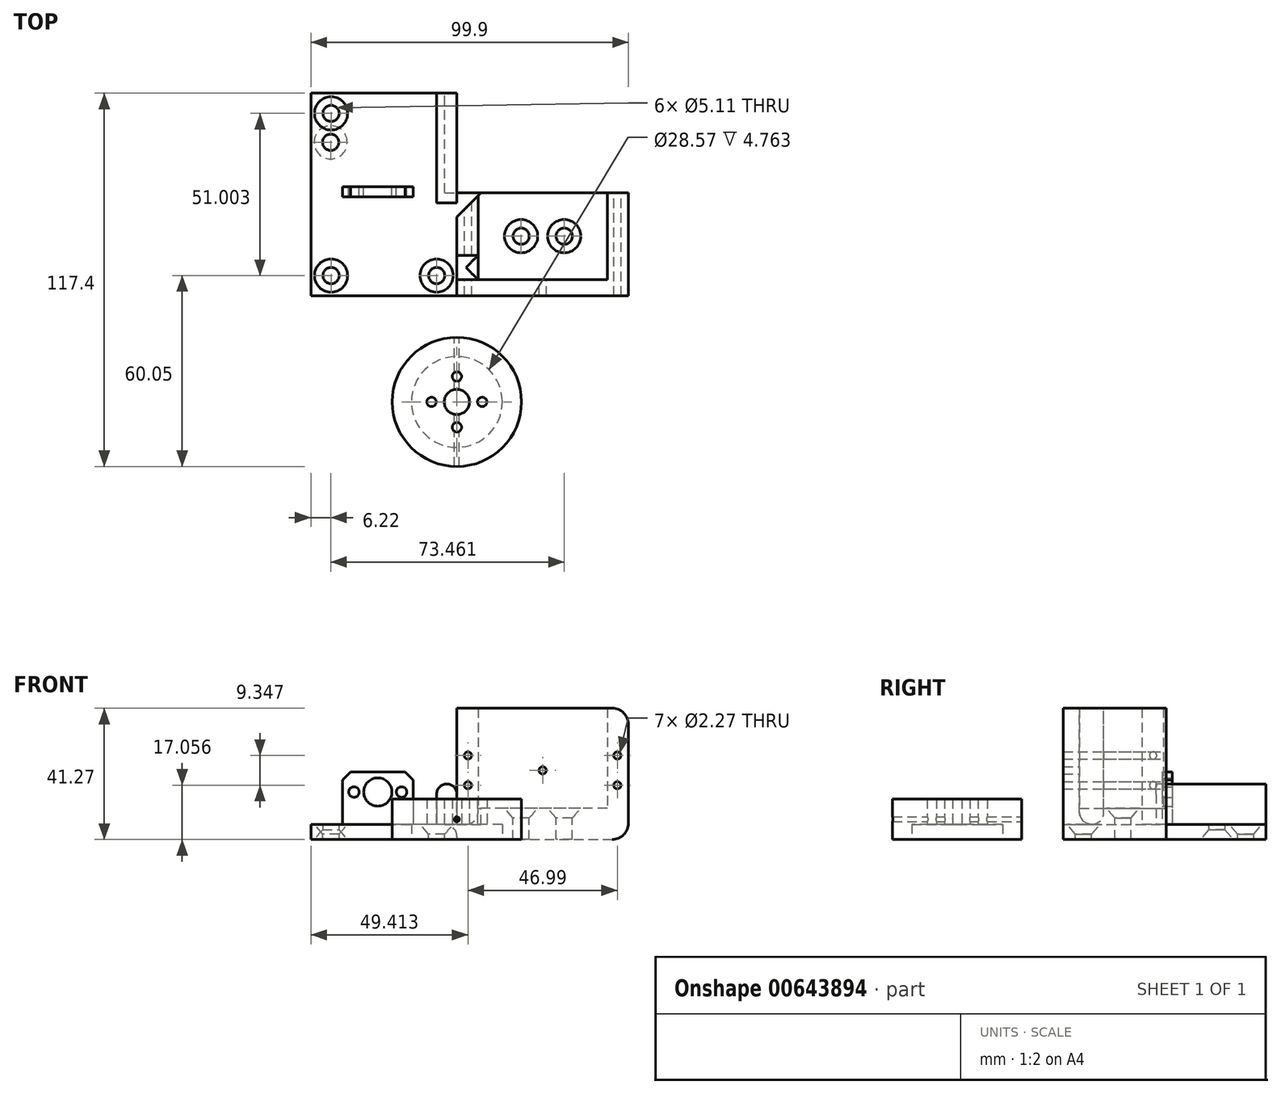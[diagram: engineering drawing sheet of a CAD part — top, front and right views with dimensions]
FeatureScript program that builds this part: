
annotation { "Feature Type Name" : "Feature", "Feature Type Description" : "" }
export const myFeature = defineFeature(function(context is Context, id is Id, definition is map)
    precondition{}
    {
        {
            var Q0;
            Q0=qCreatedBy(makeId("Top.planeOp"),FACE);
            var sketch = newSketch(context, id + "F0", { "sketchPlane" : qUnion([Q0])});
            skLineSegment(sketch, "E0.bottom", {"start": v(0, 0) * mm, "end": v(-45.92, 0) * mm});
            skLineSegment(sketch, "E0.top", {"start": v(0, 63.7) * mm, "end": v(-45.92, 63.7) * mm});
            skLineSegment(sketch, "E0.left", {"start": v(0, 0) * mm, "end": v(0, 63.7) * mm});
            skLineSegment(sketch, "E0.right", {"start": v(-45.92, 0) * mm, "end": v(-45.92, 63.7) * mm});
            skLineSegment(sketch, "E1.bottom", {"start": v(0, 32.38) * mm, "end": v(53.98, 32.38) * mm});
            skLineSegment(sketch, "E1.top", {"start": v(0, 0) * mm, "end": v(53.97, 0) * mm});
            skLineSegment(sketch, "E1.left", {"start": v(0, 32.38) * mm, "end": v(0, 0) * mm});
            skLineSegment(sketch, "E1.right", {"start": v(53.97, 32.38) * mm, "end": v(53.97, 0) * mm});
            skSolve(sketch);
        }
        {
            var Q0;
            Q0=makeQuery(id+"F0.imprint","IMPRINT",FACE,{"disambiguationData":[TD([[makeQuery(id+"F0.imprint","IMPRINT",EDGE,{"derivedFrom":sQuery(id+"F0.wireOp",EDGE,"E1.bottom")}),-1.0]])]});
            extrude(context, id + "F1", {"entities" : qUnion([Q0]), "depth" : 41.27 * mm, "offsetDistance" : 25.4 * mm});
        }
        {
            var Q0;
            Q0=makeQuery(id+"F0.imprint","IMPRINT",FACE,{"disambiguationData":[TD([[makeQuery(id+"F0.imprint","IMPRINT",EDGE,{"derivedFrom":sQuery(id+"F0.wireOp",EDGE,"E0.bottom")}),-1.0]])]});
            extrude(context, id + "F2", {"entities" : qUnion([Q0]), "operationType" : NewBodyOperationType.ADD, "depth" : 4.76 * mm, "offsetDistance" : 25.4 * mm});
        }
        {
            var Q0;
            Q0=makeQuery(id+"F1.opExtrude","SWEPT_FACE",FACE,{"disambiguationData":[OSD([sQuery(id+"F0.wireOp",EDGE,"E1.bottom")])]});
            var sketch = newSketch(context, id + "F3", { "sketchPlane" : qUnion([Q0])});
            skLineSegment(sketch, "E2.bottom", {"start": v(-47.3, 41.28) * mm, "end": v(-6.67, 41.28) * mm});
            skLineSegment(sketch, "E2.top", {"start": v(-47.3, 9.82) * mm, "end": v(-6.67, 9.82) * mm});
            skLineSegment(sketch, "E2.left", {"start": v(-47.3, 41.27) * mm, "end": v(-47.3, 9.82) * mm});
            skLineSegment(sketch, "E2.right", {"start": v(-6.67, 41.28) * mm, "end": v(-6.67, 9.82) * mm});
            skLineSegment(sketch, "E3", {"start": v(8.6, 23.02) * mm, "end": v(0, 23.02) * mm, "construction": true});
            skPoint(sketch, "E4", {"position": v(-26.99, 41.28) * mm});
            skLineSegment(sketch, "E5", {"start": v(-47.3, 21.73) * mm, "end": v(-6.67, 21.73) * mm, "construction": true});
            skLineSegment(sketch, "E6", {"start": v(-47.3, 17.06) * mm, "end": v(-50.48, 17.06) * mm, "construction": true});
            skLineSegment(sketch, "E7", {"start": v(-26.99, 41.28) * mm, "end": v(-26.99, 9.82) * mm, "construction": true});
            skLineSegment(sketch, "E8.MirrorCS", {"start": v(-47.3, 26.4) * mm, "end": v(-50.48, 26.4) * mm, "construction": true});
            skLineSegment(sketch, "E9.MirrorCS", {"start": v(-6.67, 26.4) * mm, "end": v(-3.5, 26.4) * mm, "construction": true});
            skLineSegment(sketch, "E10.MirrorCS", {"start": v(-6.67, 17.06) * mm, "end": v(-3.5, 17.06) * mm, "construction": true});
            skPoint(sketch, "E11", {"position": v(-26.99, 21.73) * mm});
            skSolve(sketch);
        }
        {
            var Q0;
            Q0=makeQuery(id+"F3.imprint","IMPRINT",FACE,{"disambiguationData":[TD([[makeQuery(id+"F3.imprint","IMPRINT",EDGE,{"derivedFrom":sQuery(id+"F3.wireOp",EDGE,"E2.bottom")}),1.0]])]});
            extrude(context, id + "F4", {"entities" : qUnion([Q0]), "operationType" : NewBodyOperationType.REMOVE, "oppositeDirection" : true, "depth" : 27.3 * mm, "offsetDistance" : 25.4 * mm});
        }
        {
            var Q0;
            Q0=makeQuery(id+"F4.boolean.opBoolean","COPY",FACE,{"derivedFrom":makeQuery(id+"F4.opExtrude","SWEPT_FACE",FACE,{"disambiguationData":[OSD([sQuery(id+"F3.wireOp",EDGE,"E2.top")])]})});
            var sketch = newSketch(context, id + "F5", { "sketchPlane" : qUnion([Q0])});
            skLineSegment(sketch, "E12", {"start": v(47.3, 18.73) * mm, "end": v(6.67, 18.73) * mm, "construction": true});
            skPoint(sketch, "E13", {"position": v(20.21, 18.73) * mm});
            skPoint(sketch, "E14", {"position": v(33.76, 18.73) * mm});
            skSolve(sketch);
        }
        {
            var Q0;
            Q0=sQuery(id+"F5.wireOp",VERTEX,"E13");
            var Q1;
            Q1=sQuery(id+"F5.wireOp",VERTEX,"E14");
            var Q2;
            Q2=makeQuery(id+"F1.opExtrude","SWEPT_BODY",BODY,{"disambiguationData":[OSD([sQuery(id+"F0.wireOp",EDGE,"E1.bottom"),sQuery(id+"F0.wireOp",EDGE,"E1.top"),sQuery(id+"F0.wireOp",EDGE,"E1.left"),sQuery(id+"F0.wireOp",EDGE,"E1.right")])]});
            hole(context, id + "F6", {"style" : HoleStyle.C_SINK, "endStyle" : HoleEndStyle.THROUGH, "standardTappedOrClearance" : lookupTablePath({ "standard" : "ANSI", "fit" : "Normal (ASME)", "size" : "#10", "type" : "Clearance" }), "standardBlindInLast" : lookupTablePath({ "fit" : "Free", "standard" : "ANSI", "size" : "#10", "type" : "Clearance" }), "holeDiameter" : 5.1 * mm, "cSinkDiameter" : 10.44 * mm, "cSinkAngle" : 82 * degree, "majorDiameter" : 6.35 * mm, "isTappedThrough" : true, "tappedDepth" : 39.45 * mm, "tapClearance" : 3, "locations" : qUnion([Q0, Q1]), "scope" : qUnion([Q2])});
        }
        {
            var Q0;
            Q0=makeQuery(id+"F2.opExtrude","CAP_FACE",FACE,{"disambiguationData":[OSD([sQuery(id+"F0.wireOp",EDGE,"E0.bottom"),sQuery(id+"F0.wireOp",EDGE,"E0.top"),sQuery(id+"F0.wireOp",EDGE,"E0.left"),sQuery(id+"F0.wireOp",EDGE,"E0.right"),sQuery(id+"F0.wireOp",EDGE,"E1.left")])],"isStart":false});
            var sketch = newSketch(context, id + "F7", { "sketchPlane" : qUnion([Q0])});
            skLineSegment(sketch, "E15", {"start": v(-39.57, 63.7) * mm, "end": v(-39.57, 0) * mm});
            skLineSegment(sketch, "E16", {"start": v(-39.57, 6.35) * mm, "end": v(0, 6.35) * mm});
            skLineSegment(sketch, "E17", {"start": v(-22.96, 63.7) * mm, "end": v(-22.96, 0) * mm, "construction": true});
            skLineSegment(sketch, "E18", {"start": v(-45.92, 31.85) * mm, "end": v(0, 31.85) * mm, "construction": true});
            skLineSegment(sketch, "E19.MirrorCS", {"start": v(-39.57, 57.35) * mm, "end": v(0, 57.35) * mm});
            skLineSegment(sketch, "E20.MirrorCS", {"start": v(-6.35, 63.7) * mm, "end": v(-6.35, 0) * mm});
            skPoint(sketch, "E21", {"position": v(-6.35, 6.35) * mm});
            skPoint(sketch, "E22", {"position": v(-6.35, 57.35) * mm});
            skSolve(sketch);
        }
        {
            var Q0;
            Q0=sQuery(id+"F7.wireOp",VERTEX,"E19.MirrorCS.start");
            var Q1;
            Q1=sQuery(id+"F7.wireOp",VERTEX,"E21");
            var Q2;
            Q2=sQuery(id+"F7.wireOp",VERTEX,"E16.start");
            var Q3;
            Q3=makeQuery(id+"F1.opExtrude","SWEPT_BODY",BODY,{"disambiguationData":[OSD([sQuery(id+"F0.wireOp",EDGE,"E1.bottom"),sQuery(id+"F0.wireOp",EDGE,"E1.top"),sQuery(id+"F0.wireOp",EDGE,"E1.left"),sQuery(id+"F0.wireOp",EDGE,"E1.right")])]});
            hole(context, id + "F8", {"style" : HoleStyle.C_SINK, "endStyle" : HoleEndStyle.THROUGH, "standardTappedOrClearance" : lookupTablePath({ "standard" : "ANSI", "fit" : "Normal (ASME)", "size" : "#10", "type" : "Clearance" }), "standardBlindInLast" : lookupTablePath({ "fit" : "Free", "standard" : "ANSI", "size" : "#10", "type" : "Clearance" }), "holeDiameter" : 5.1 * mm, "cSinkDiameter" : 10.44 * mm, "cSinkAngle" : 82 * degree, "majorDiameter" : 6.35 * mm, "isTappedThrough" : true, "tappedDepth" : 39.45 * mm, "tapClearance" : 3, "locations" : qUnion([Q0, Q1, Q2]), "scope" : qUnion([Q3])});
        }
        {
            var Q0;
            Q0=sQuery(id+"F3.wireOp",VERTEX,"E9.MirrorCS.end");
            var Q1;
            Q1=sQuery(id+"F3.wireOp",VERTEX,"E10.MirrorCS.end");
            var Q2;
            Q2=sQuery(id+"F3.wireOp",VERTEX,"E8.MirrorCS.end");
            var Q3;
            Q3=sQuery(id+"F3.wireOp",VERTEX,"E6.end");
            var Q4;
            Q4=sQuery(id+"F3.wireOp",VERTEX,"E11");
            var Q5;
            Q5=makeQuery(id+"F1.opExtrude","SWEPT_BODY",BODY,{"disambiguationData":[OSD([sQuery(id+"F0.wireOp",EDGE,"E1.bottom"),sQuery(id+"F0.wireOp",EDGE,"E1.top"),sQuery(id+"F0.wireOp",EDGE,"E1.left"),sQuery(id+"F0.wireOp",EDGE,"E1.right")])]});
            hole(context, id + "F9", {"style" : HoleStyle.SIMPLE, "endStyle" : HoleEndStyle.BLIND, "holeDiameter" : 2.27 * mm, "majorDiameter" : 6.35 * mm, "holeDepth" : 50.8 * mm, "isTappedThrough" : true, "tappedDepth" : 39.45 * mm, "tapClearance" : 3, "locations" : qUnion([Q0, Q1, Q2, Q3, Q4]), "scope" : qUnion([Q5])});
        }
        {
            var Q0;
            Q0=makeQuery(id+"F1.opExtrude","CAP_FACE",FACE,{"disambiguationData":[OSD([sQuery(id+"F0.wireOp",EDGE,"E1.bottom"),sQuery(id+"F0.wireOp",EDGE,"E1.top"),sQuery(id+"F0.wireOp",EDGE,"E1.left"),sQuery(id+"F0.wireOp",EDGE,"E1.right")])],"isStart":false});
            var sketch = newSketch(context, id + "F10", { "sketchPlane" : qUnion([Q0])});
            skLineSegment(sketch, "E23.bottom", {"start": v(6.67, 5.08) * mm, "end": v(0, 5.08) * mm});
            skLineSegment(sketch, "E23.top", {"start": v(6.67, 12.72) * mm, "end": v(0, 12.72) * mm});
            skLineSegment(sketch, "E23.left", {"start": v(6.67, 5.08) * mm, "end": v(6.67, 12.72) * mm});
            skLineSegment(sketch, "E23.right", {"start": v(0, 5.08) * mm, "end": v(0, 12.72) * mm});
            skSolve(sketch);
        }
        {
            var Q0;
            Q0=makeQuery(id+"F10.imprint","IMPRINT",FACE,{"disambiguationData":[TD([[makeQuery(id+"F10.imprint","IMPRINT",EDGE,{"derivedFrom":sQuery(id+"F10.wireOp",EDGE,"E23.bottom")}),-1.0]])]});
            var Q1;
            Q1=makeQuery(id+"F2.opExtrude","CAP_FACE",FACE,{"disambiguationData":[OSD([sQuery(id+"F0.wireOp",EDGE,"E0.bottom"),sQuery(id+"F0.wireOp",EDGE,"E0.top"),sQuery(id+"F0.wireOp",EDGE,"E0.left"),sQuery(id+"F0.wireOp",EDGE,"E0.right"),sQuery(id+"F0.wireOp",EDGE,"E1.left")])],"isStart":false});
            extrude(context, id + "F11", {"entities" : qUnion([Q0]), "operationType" : NewBodyOperationType.REMOVE, "endBound" : BoundingType.UP_TO_SURFACE, "oppositeDirection" : true, "depth" : 25.4 * mm, "endBoundEntityFace" : qUnion([Q1]), "offsetDistance" : 25.4 * mm});
        }
        {
            var Q0;
            {var subQ0=sQuery(id+"F0.wireOp",EDGE,"E1.bottom");var subQ1=sQuery(id+"F0.wireOp",EDGE,"E1.left");var subQ2=sQuery(id+"F0.wireOp",EDGE,"E0.left");Q0=makeQuery(id+"F2.boolean.opBoolean","SPLIT",EDGE,{"disambiguationData":[topologyDisambiguationEdgeConnected([makeQuery(id+"F2.opExtrude","SWEPT_FACE",FACE,{"disambiguationData":[OSD([subQ2,subQ1])]})])],"derivedFrom":makeQuery(id+"F1.opExtrude","SWEPT_EDGE",EDGE,{"disambiguationData":[OSD([subQ2,subQ0,subQ1])]})});}
            chamfer(context, id + "F12", {"entities" : qUnion([Q0]), "width" : 7.62 * mm, "tangentPropagation" : true});
        }
        {
            var Q0;
            Q0=makeQuery(id+"F11.boolean.opBoolean","COPY",EDGE,{"derivedFrom":makeQuery(id+"F11.opExtrude","CAP_EDGE",EDGE,{"disambiguationData":[OSD([sQuery(id+"F10.wireOp",EDGE,"E23.top")])],"isStart":false})});
            var Q1;
            Q1=makeQuery(id+"F11.boolean.opBoolean","COPY",EDGE,{"derivedFrom":makeQuery(id+"F11.opExtrude","CAP_EDGE",EDGE,{"disambiguationData":[OSD([sQuery(id+"F10.wireOp",EDGE,"E23.bottom")])],"isStart":false})});
            var Q2;
            {var subQ0=sQuery(id+"F0.wireOp",EDGE,"E1.left");var subQ1=sQuery(id+"F0.wireOp",EDGE,"E0.left");var subQ4=makeQuery(id+"F1.opExtrude","SWEPT_FACE",FACE,{"disambiguationData":[OSD([subQ0])]});Q2=makeQuery(id+"F11.boolean.opBoolean","SPLIT",EDGE,{"disambiguationData":[TD([makeQuery(id+"F1.opExtrude","SWEPT_FACE",FACE,{"disambiguationData":[OSD([sQuery(id+"F0.wireOp",EDGE,"E1.bottom")])]})])],"derivedFrom":makeQuery(id+"F2.boolean.opBoolean","SPLIT",EDGE,{"disambiguationData":[topologyDisambiguationEdgeConnected([subQ4])],"derivedFrom":makeQuery(id+"F2.opExtrude","CAP_EDGE",EDGE,{"disambiguationData":[OSD([subQ1,subQ0])],"isStart":false})})});}
            var Q3;
            {var subQ1=sQuery(id+"F0.wireOp",EDGE,"E1.left");var subQ2=makeQuery(id+"F1.opExtrude","SWEPT_FACE",FACE,{"disambiguationData":[OSD([subQ1])]});var subQ3=sQuery(id+"F0.wireOp",EDGE,"E0.left");Q3=makeQuery(id+"F11.boolean.opBoolean","SPLIT",EDGE,{"disambiguationData":[TD([makeQuery(id+"F1.opExtrude","SWEPT_FACE",FACE,{"disambiguationData":[OSD([sQuery(id+"F0.wireOp",EDGE,"E1.top")])]})])],"derivedFrom":makeQuery(id+"F2.boolean.opBoolean","SPLIT",EDGE,{"disambiguationData":[topologyDisambiguationEdgeConnected([subQ2])],"derivedFrom":makeQuery(id+"F2.opExtrude","CAP_EDGE",EDGE,{"disambiguationData":[OSD([subQ3,subQ1])],"isStart":false})})});}
            var Q4;
            Q4=makeQuery(id+"F11.boolean.opBoolean","COPY",EDGE,{"derivedFrom":makeQuery(id+"F11.opExtrude","CAP_EDGE",EDGE,{"disambiguationData":[OSD([sQuery(id+"F10.wireOp",EDGE,"E23.left")])],"isStart":false})});
            var Q5;
            {var subQ0=sQuery(id+"F0.wireOp",EDGE,"E1.left");var subQ1=sQuery(id+"F0.wireOp",EDGE,"E0.left");Q5=makeQuery(id+"F12.opChamfer","TWEAK_EDGE",EDGE,{"derivedFrom":[makeQuery(id+"F2.boolean.opBoolean","TWEAK_VERTEX",VERTEX,{"derivedFrom":[makeQuery(id+"F1.opExtrude","SWEPT_FACE",FACE,{"disambiguationData":[OSD([sQuery(id+"F0.wireOp",EDGE,"E1.bottom")])]}),makeQuery(id+"F1.opExtrude","SWEPT_FACE",FACE,{"disambiguationData":[OSD([subQ0])]}),makeQuery(id+"F2.opExtrude","CAP_FACE",FACE,{"disambiguationData":[OSD([sQuery(id+"F0.wireOp",EDGE,"E0.bottom"),sQuery(id+"F0.wireOp",EDGE,"E0.top"),subQ1,sQuery(id+"F0.wireOp",EDGE,"E0.right"),subQ0])],"isStart":false}),makeQuery(id+"F2.opExtrude","SWEPT_FACE",FACE,{"disambiguationData":[OSD([subQ1,subQ0])]})]})]});}
            fillet(context, id + "F13", {"entities" : qUnion([Q0, Q1, Q2, Q3, Q4, Q5]), "radius" : 3.8 * mm, "tangentPropagation" : true, "allowEdgeOverflow" : false});
        }
        {
            var Q0;
            Q0=makeQuery(id+"F1.opExtrude","CAP_EDGE",EDGE,{"disambiguationData":[OSD([sQuery(id+"F0.wireOp",EDGE,"E1.right")])],"isStart":false});
            var Q1;
            Q1=makeQuery(id+"F1.opExtrude","CAP_EDGE",EDGE,{"disambiguationData":[OSD([sQuery(id+"F0.wireOp",EDGE,"E1.right")])],"isStart":true});
            var Q2;
            {var subQ0=sQuery(id+"F0.wireOp",EDGE,"E1.bottom");var subQ1=sQuery(id+"F0.wireOp",EDGE,"E1.left");Q2=makeQuery(id+"F11.boolean.opBoolean","SPLIT",EDGE,{"disambiguationData":[TD([makeQuery(id+"F1.opExtrude","SWEPT_FACE",FACE,{"disambiguationData":[OSD([subQ0])]})])],"derivedFrom":makeQuery(id+"F1.opExtrude","CAP_EDGE",EDGE,{"disambiguationData":[OSD([subQ1])],"isStart":false})});}
            var Q3;
            {var subQ0=sQuery(id+"F0.wireOp",EDGE,"E1.left");var subQ1=sQuery(id+"F0.wireOp",EDGE,"E1.top");Q3=makeQuery(id+"F11.boolean.opBoolean","SPLIT",EDGE,{"disambiguationData":[TD([makeQuery(id+"F1.opExtrude","SWEPT_FACE",FACE,{"disambiguationData":[OSD([subQ1])]})])],"derivedFrom":makeQuery(id+"F1.opExtrude","CAP_EDGE",EDGE,{"disambiguationData":[OSD([subQ0])],"isStart":false})});}
            fillet(context, id + "F14", {"entities" : qUnion([Q0, Q1, Q2, Q3]), "radius" : 5.08 * mm, "tangentPropagation" : true, "allowEdgeOverflow" : false});
        }
        {
            var Q0;
            Q0=makeQuery(id+"F13.opFillet","SPLIT",FACE,{"disambiguationData":[OD(1.0)],"derivedFrom":makeQuery(id+"F11.boolean.opBoolean","MERGE",FACE,{"derivedFrom":[makeQuery(id+"F2.opExtrude","CAP_FACE",FACE,{"disambiguationData":[OSD([sQuery(id+"F0.wireOp",EDGE,"E0.bottom"),sQuery(id+"F0.wireOp",EDGE,"E0.top"),sQuery(id+"F0.wireOp",EDGE,"E0.left"),sQuery(id+"F0.wireOp",EDGE,"E0.right"),sQuery(id+"F0.wireOp",EDGE,"E1.left")])],"isStart":false})],"fromTools":[makeQuery(id+"F11.opExtrude","CAP_FACE",FACE,{"disambiguationData":[OSD([sQuery(id+"F10.wireOp",EDGE,"E23.bottom"),sQuery(id+"F10.wireOp",EDGE,"E23.top"),sQuery(id+"F10.wireOp",EDGE,"E23.left"),sQuery(id+"F10.wireOp",EDGE,"E23.right")])],"isStart":false})]})});
            var sketch = newSketch(context, id + "F15", { "sketchPlane" : qUnion([Q0])});
            skLineSegment(sketch, "E24.bottom", {"start": v(-35.98, 34.29) * mm, "end": v(-13.75, 34.3) * mm});
            skLineSegment(sketch, "E24.top", {"start": v(-35.98, 31.12) * mm, "end": v(-13.75, 31.12) * mm});
            skLineSegment(sketch, "E24.left", {"start": v(-35.98, 34.29) * mm, "end": v(-35.98, 31.12) * mm});
            skLineSegment(sketch, "E24.right", {"start": v(-13.75, 34.3) * mm, "end": v(-13.75, 31.12) * mm});
            skLineSegment(sketch, "E25", {"start": v(-24.87, 31.12) * mm, "end": v(-24.87, 0) * mm, "construction": true});
            skLineSegment(sketch, "E26", {"start": v(-24.87, 34.3) * mm, "end": v(-24.87, 48.26) * mm, "construction": true});
            skLineSegment(sketch, "E27", {"start": v(-24.87, 48.26) * mm, "end": v(-39.7, 48.26) * mm, "construction": true});
            skSolve(sketch);
        }
        {
            var Q0;
            {var subQ0=sQuery(id+"F0.wireOp",EDGE,"E1.left");Q0=makeQuery(id+"F2.boolean.opBoolean","MERGE",FACE,{"derivedFrom":[makeQuery(id+"F1.opExtrude","CAP_FACE",FACE,{"disambiguationData":[OSD([sQuery(id+"F0.wireOp",EDGE,"E1.bottom"),sQuery(id+"F0.wireOp",EDGE,"E1.top"),subQ0,sQuery(id+"F0.wireOp",EDGE,"E1.right")])],"isStart":true}),makeQuery(id+"F2.opExtrude","CAP_FACE",FACE,{"disambiguationData":[OSD([sQuery(id+"F0.wireOp",EDGE,"E0.bottom"),sQuery(id+"F0.wireOp",EDGE,"E0.top"),sQuery(id+"F0.wireOp",EDGE,"E0.left"),sQuery(id+"F0.wireOp",EDGE,"E0.right"),subQ0])],"isStart":true})]});}
            var sketch = newSketch(context, id + "F16", { "sketchPlane" : qUnion([Q0])});
            skPoint(sketch, "E28", {"position": v(-39.7, -48.26) * mm});
            skSolve(sketch);
        }
        {
            var Q0;
            Q0=sQuery(id+"F16.wireOp",VERTEX,"E28");
            var Q1;
            Q1=makeQuery(id+"F1.opExtrude","SWEPT_BODY",BODY,{"disambiguationData":[OSD([sQuery(id+"F0.wireOp",EDGE,"E1.bottom"),sQuery(id+"F0.wireOp",EDGE,"E1.top"),sQuery(id+"F0.wireOp",EDGE,"E1.left"),sQuery(id+"F0.wireOp",EDGE,"E1.right")])]});
            hole(context, id + "F17", {"style" : HoleStyle.C_SINK, "endStyle" : HoleEndStyle.THROUGH, "standardTappedOrClearance" : lookupTablePath({ "standard" : "ANSI", "fit" : "Normal (ASME)", "size" : "#10", "type" : "Clearance" }), "standardBlindInLast" : lookupTablePath({ "fit" : "Free", "standard" : "ANSI", "size" : "#10", "type" : "Clearance" }), "holeDiameter" : 5.1 * mm, "cSinkDiameter" : 10.44 * mm, "cSinkAngle" : 82 * degree, "majorDiameter" : 6.35 * mm, "isTappedThrough" : true, "tappedDepth" : 39.45 * mm, "tapClearance" : 3, "locations" : qUnion([Q0]), "scope" : qUnion([Q1])});
        }
        {
            var Q0;
            Q0=makeQuery(id+"F15.imprint","IMPRINT",FACE,{"disambiguationData":[TD([[makeQuery(id+"F15.imprint","IMPRINT",EDGE,{"derivedFrom":sQuery(id+"F15.wireOp",EDGE,"E24.bottom")}),-1.0]])]});
            extrude(context, id + "F18", {"entities" : qUnion([Q0]), "operationType" : NewBodyOperationType.ADD, "depth" : 16.5 * mm, "offsetDistance" : 25.4 * mm});
        }
        {
            var Q0;
            Q0=makeQuery(id+"F18.opExtrude","CAP_EDGE",EDGE,{"disambiguationData":[OSD([sQuery(id+"F15.wireOp",EDGE,"E24.left")])],"isStart":false});
            var Q1;
            Q1=makeQuery(id+"F18.opExtrude","CAP_EDGE",EDGE,{"disambiguationData":[OSD([sQuery(id+"F15.wireOp",EDGE,"E24.right")])],"isStart":false});
            var Q2;
            Q2=makeQuery(id+"F18.opExtrude","CAP_EDGE",EDGE,{"disambiguationData":[OSD([sQuery(id+"F15.wireOp",EDGE,"E24.bottom")])],"isStart":true});
            var Q3;
            Q3=makeQuery(id+"F18.opExtrude","CAP_EDGE",EDGE,{"disambiguationData":[OSD([sQuery(id+"F15.wireOp",EDGE,"E24.left")])],"isStart":true});
            var Q4;
            Q4=makeQuery(id+"F18.opExtrude","CAP_EDGE",EDGE,{"disambiguationData":[OSD([sQuery(id+"F15.wireOp",EDGE,"E24.right")])],"isStart":true});
            chamfer(context, id + "F19", {"entities" : qUnion([Q0, Q1, Q2, Q3, Q4]), "width" : 2.54 * mm, "tangentPropagation" : true});
        }
        {
            var Q0;
            Q0=makeQuery(id+"F18.opExtrude","SWEPT_FACE",FACE,{"disambiguationData":[OSD([sQuery(id+"F15.wireOp",EDGE,"E24.bottom")])]});
            var sketch = newSketch(context, id + "F20", { "sketchPlane" : qUnion([Q0])});
            skLineSegment(sketch, "E29", {"start": v(24.87, 21.27) * mm, "end": v(24.87, 7.3) * mm, "construction": true});
            skCircle(sketch, "E30", {"center": v(24.87, 14.92) * mm, "radius": 4.45 * mm});
            skLineSegment(sketch, "E31", {"start": v(24.87, 14.92) * mm, "end": v(17.37, 14.92) * mm});
            skLineSegment(sketch, "E32.MirrorCS", {"start": v(24.87, 14.92) * mm, "end": v(32.36, 14.92) * mm});
            skSolve(sketch);
        }
        {
            var Q0;
            Q0=sQuery(id+"F20.wireOp",VERTEX,"E32.MirrorCS.end");
            var Q1;
            Q1=sQuery(id+"F20.wireOp",VERTEX,"E31.end");
            var Q2;
            Q2=makeQuery(id+"F1.opExtrude","SWEPT_BODY",BODY,{"disambiguationData":[OSD([sQuery(id+"F0.wireOp",EDGE,"E1.bottom"),sQuery(id+"F0.wireOp",EDGE,"E1.top"),sQuery(id+"F0.wireOp",EDGE,"E1.left"),sQuery(id+"F0.wireOp",EDGE,"E1.right")])]});
            hole(context, id + "F21", {"style" : HoleStyle.SIMPLE, "endStyle" : HoleEndStyle.BLIND, "standardTappedOrClearance" : lookupTablePath({ "standard" : "ISO", "fit" : "Normal", "size" : "M3", "type" : "Clearance" }), "standardBlindInLast" : lookupTablePath({ "fit" : "Standard", "standard" : "ISO", "size" : "M3", "type" : "Clearance" }), "holeDiameter" : 3.3 * mm, "majorDiameter" : 6.35 * mm, "holeDepth" : 50.8 * mm, "isTappedThrough" : true, "tappedDepth" : 39.45 * mm, "tapClearance" : 3, "locations" : qUnion([Q0, Q1]), "scope" : qUnion([Q2])});
        }
        {
            var Q0;
            Q0=qSketchRegion(id+"F20",true);
            extrude(context, id + "F22", {"entities" : qUnion([Q0]), "operationType" : NewBodyOperationType.REMOVE, "oppositeDirection" : true, "depth" : 25.4 * mm, "offsetDistance" : 25.4 * mm});
        }
        {
            var Q0;
            Q0=qCreatedBy(makeId("Top.planeOp"),FACE);
            var sketch = newSketch(context, id + "F23", { "sketchPlane" : qUnion([Q0])});
            skCircle(sketch, "E33", {"center": v(0, -33.38) * mm, "radius": 3.97 * mm});
            skCircle(sketch, "E34", {"center": v(0, -33.38) * mm, "radius": 7.98 * mm, "construction": true});
            skLineSegment(sketch, "E35", {"start": v(0, -25.4) * mm, "end": v(0, -41.35) * mm, "construction": true});
            skLineSegment(sketch, "E36", {"start": v(7.98, -33.38) * mm, "end": v(-7.98, -33.38) * mm, "construction": true});
            skLineSegment(sketch, "E37", {"start": v(0, 0) * mm, "end": v(0, -25.4) * mm, "construction": true});
            skCircle(sketch, "E38", {"center": v(0, -33.38) * mm, "radius": 11.43 * mm, "construction": true});
            skCircle(sketch, "E39", {"center": v(0, -33.38) * mm, "radius": 20.32 * mm});
            skCircle(sketch, "E40", {"center": v(0, -33.38) * mm, "radius": 14.29 * mm});
            skSolve(sketch);
        }
        {
            var Q0;
            Q0=makeQuery(id+"F23.imprint","IMPRINT",FACE,{"disambiguationData":[TD([[makeQuery(id+"F23.imprint","IMPRINT",EDGE,{"derivedFrom":sQuery(id+"F23.wireOp",EDGE,"E39")}),1.0]])]});
            var Q1;
            Q1=makeQuery(id+"F23.imprint","IMPRINT",FACE,{"disambiguationData":[TD([[makeQuery(id+"F23.imprint","IMPRINT",EDGE,{"derivedFrom":sQuery(id+"F23.wireOp",EDGE,"E33")}),-1.0]])]});
            extrude(context, id + "F24", {"entities" : qUnion([Q0, Q1]), "depth" : 12.7 * mm, "offsetDistance" : 25.4 * mm});
        }
        {
            var Q0;
            Q0=makeQuery(id+"F23.imprint","IMPRINT",FACE,{"disambiguationData":[TD([[makeQuery(id+"F23.imprint","IMPRINT",EDGE,{"derivedFrom":sQuery(id+"F23.wireOp",EDGE,"E33")}),-1.0]])]});
            extrude(context, id + "F25", {"entities" : qUnion([Q0]), "operationType" : NewBodyOperationType.REMOVE, "depth" : 4.76 * mm, "offsetDistance" : 25.4 * mm});
        }
        {
            var Q0;
            Q0=sQuery(id+"F23.wireOp",VERTEX,"E36.end");
            var Q1;
            Q1=sQuery(id+"F23.wireOp",VERTEX,"E36.start");
            var Q2;
            Q2=sQuery(id+"F23.wireOp",VERTEX,"E35.end");
            var Q3;
            Q3=sQuery(id+"F23.wireOp",VERTEX,"E35.start");
            var Q4;
            Q4=makeQuery(id+"F24.opExtrude","SWEPT_BODY",BODY,{"disambiguationData":[OSD([sQuery(id+"F23.wireOp",EDGE,"E39"),sQuery(id+"F23.wireOp",EDGE,"E40")])]});
            hole(context, id + "F26", {"style" : HoleStyle.SIMPLE, "endStyle" : HoleEndStyle.THROUGH, "oppositeDirection" : true, "standardTappedOrClearance" : lookupTablePath({ "standard" : "ANSI", "engagement" : "50%", "pitch" : "32 tpi", "size" : "#6", "type" : "Tapped" }), "standardBlindInLast" : lookupTablePath({ "standard" : "ANSI", "engagement" : "50%", "pitch" : "32 tpi", "size" : "#6", "type" : "Tapped" }), "holeDiameter" : 2.95 * mm, "majorDiameter" : 3.5 * mm, "showTappedDepth" : true, "isTappedThrough" : true, "tappedDepth" : 39.45 * mm, "tapClearance" : 3, "locations" : qUnion([Q0, Q1, Q2, Q3]), "scope" : qUnion([Q4])});
        }
        {
            var Q0;
            Q0=qCreatedBy(makeId("Front.planeOp"),FACE);
            var sketch = newSketch(context, id + "F27", { "sketchPlane" : qUnion([Q0])});
            skLineSegment(sketch, "E41", {"start": v(0, 12.7) * mm, "end": v(0, 0) * mm});
            skPoint(sketch, "E42", {"position": v(0, 6.35) * mm});
            skSolve(sketch);
        }
        {
            var Q0;
            Q0=sQuery(id+"F27.wireOp",VERTEX,"E42");
            var Q1;
            Q1=makeQuery(id+"F24.opExtrude","SWEPT_BODY",BODY,{"disambiguationData":[OSD([sQuery(id+"F23.wireOp",EDGE,"E39"),sQuery(id+"F23.wireOp",EDGE,"E40")])]});
            hole(context, id + "F28", {"style" : HoleStyle.SIMPLE, "endStyle" : HoleEndStyle.THROUGH, "oppositeDirection" : true, "holeDiameter" : 1.59 * mm, "majorDiameter" : 3.5 * mm, "isTappedThrough" : true, "tappedDepth" : 39.45 * mm, "tapClearance" : 3, "locations" : qUnion([Q0]), "scope" : qUnion([Q1])});
        }
        {
            var Q0;
            Q0=makeQuery(id+"F13.opFillet","SPLIT",FACE,{"disambiguationData":[OD(1.0)],"derivedFrom":makeQuery(id+"F11.boolean.opBoolean","MERGE",FACE,{"derivedFrom":[makeQuery(id+"F2.opExtrude","CAP_FACE",FACE,{"disambiguationData":[OSD([sQuery(id+"F0.wireOp",EDGE,"E0.bottom"),sQuery(id+"F0.wireOp",EDGE,"E0.top"),sQuery(id+"F0.wireOp",EDGE,"E0.left"),sQuery(id+"F0.wireOp",EDGE,"E0.right"),sQuery(id+"F0.wireOp",EDGE,"E1.left")])],"isStart":false})],"fromTools":[makeQuery(id+"F11.opExtrude","CAP_FACE",FACE,{"disambiguationData":[OSD([sQuery(id+"F10.wireOp",EDGE,"E23.bottom"),sQuery(id+"F10.wireOp",EDGE,"E23.top"),sQuery(id+"F10.wireOp",EDGE,"E23.left"),sQuery(id+"F10.wireOp",EDGE,"E23.right")])],"isStart":false})]})});
            var sketch = newSketch(context, id + "F29", { "sketchPlane" : qUnion([Q0])});
            skLineSegment(sketch, "E43.bottom", {"start": v(0, 63.7) * mm, "end": v(-6.35, 63.7) * mm});
            skLineSegment(sketch, "E43.top", {"start": v(0, 29.2) * mm, "end": v(-6.35, 29.2) * mm});
            skLineSegment(sketch, "E43.left", {"start": v(0, 63.7) * mm, "end": v(0, 29.2) * mm});
            skLineSegment(sketch, "E43.right", {"start": v(-6.35, 63.7) * mm, "end": v(-6.35, 29.2) * mm});
            skSolve(sketch);
        }
        {
            var Q0;
            Q0=qSketchRegion(id+"F29",true);
            extrude(context, id + "F30", {"entities" : qUnion([Q0]), "operationType" : NewBodyOperationType.ADD, "depth" : 12.7 * mm, "offsetDistance" : 25.4 * mm});
        }
        {
            var Q0;
            {var subQ0=sQuery(id+"F29.wireOp",EDGE,"E43.left");Q0=makeQuery(id+"F30.boolean.opBoolean","SPLIT",EDGE,{"disambiguationData":[topologyDisambiguationEdgeConnected([makeQuery(id+"F30.opExtrude","SWEPT_FACE",FACE,{"disambiguationData":[OSD([subQ0])]})])],"derivedFrom":makeQuery(id+"F30.opExtrude","CAP_EDGE",EDGE,{"disambiguationData":[OSD([subQ0])],"isStart":false})});}
            var Q1;
            Q1=makeQuery(id+"F30.opExtrude","CAP_EDGE",EDGE,{"disambiguationData":[OSD([sQuery(id+"F29.wireOp",EDGE,"E43.right")])],"isStart":false});
            fillet(context, id + "F31", {"entities" : qUnion([Q0, Q1]), "radius" : 3.17 * mm, "tangentPropagation" : true, "allowEdgeOverflow" : false});
        }
    });
